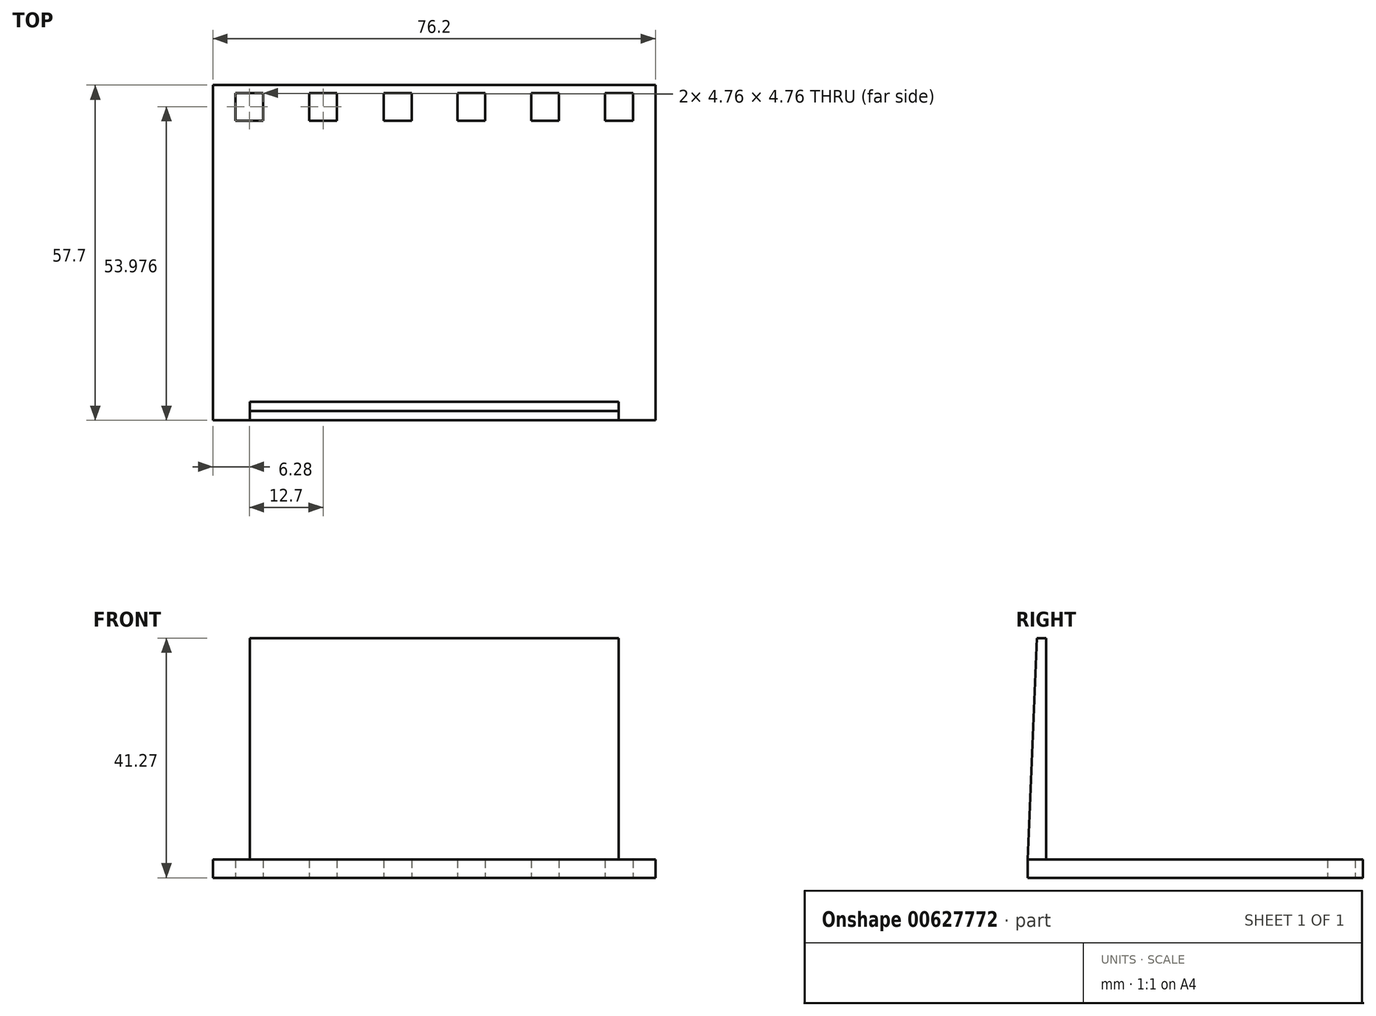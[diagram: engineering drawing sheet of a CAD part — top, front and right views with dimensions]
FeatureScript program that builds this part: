
annotation { "Feature Type Name" : "Feature", "Feature Type Description" : "" }
export const myFeature = defineFeature(function(context is Context, id is Id, definition is map)
    precondition{}
    {
        {
            var Q0;
            Q0=qCreatedBy(makeId("Top.planeOp"),FACE);
            var sketch = newSketch(context, id + "F0", { "sketchPlane" : qUnion([Q0])});
            skLineSegment(sketch, "E0.bottom", {"start": v(38.1, 31.75) * mm, "end": v(-38.1, 31.75) * mm});
            skLineSegment(sketch, "E0.top", {"start": v(38.1, -31.75) * mm, "end": v(-38.1, -31.75) * mm});
            skLineSegment(sketch, "E0.left", {"start": v(38.1, 31.75) * mm, "end": v(38.1, -31.75) * mm});
            skLineSegment(sketch, "E0.right", {"start": v(-38.1, 31.75) * mm, "end": v(-38.1, -31.75) * mm});
            skPoint(sketch, "E0.middle", {"position": v(0, 0) * mm});
            skLineSegment(sketch, "E1.bottom", {"start": v(-34.2, 27.79) * mm, "end": v(-29.44, 27.79) * mm});
            skLineSegment(sketch, "E1.top", {"start": v(-34.2, 23.03) * mm, "end": v(-29.44, 23.03) * mm});
            skLineSegment(sketch, "E1.left", {"start": v(-34.2, 27.79) * mm, "end": v(-34.2, 23.03) * mm});
            skLineSegment(sketch, "E1.right", {"start": v(-29.44, 27.79) * mm, "end": v(-29.44, 23.03) * mm});
            skLineSegment(sketch, "E2", {"start": v(-34.2, 27.79) * mm, "end": v(-38.1, 27.79) * mm});
            skLineSegment(sketch, "E3", {"start": v(-34.2, 27.79) * mm, "end": v(-34.2, 31.75) * mm});
            skLineSegment(sketch, "E4", {"start": v(-29.44, 27.79) * mm, "end": v(-21.5, 27.79) * mm});
            skLineSegment(sketch, "E5.bottom", {"start": v(-21.5, 27.79) * mm, "end": v(-16.74, 27.79) * mm});
            skLineSegment(sketch, "E5.top", {"start": v(-21.5, 23.03) * mm, "end": v(-16.74, 23.03) * mm});
            skLineSegment(sketch, "E5.left", {"start": v(-21.5, 27.79) * mm, "end": v(-21.5, 23.03) * mm});
            skLineSegment(sketch, "E5.right", {"start": v(-16.74, 27.79) * mm, "end": v(-16.74, 23.03) * mm});
            skLineSegment(sketch, "E6", {"start": v(-34.2, 23.03) * mm, "end": v(-34.2, 15.09) * mm});
            skLineSegment(sketch, "E7.left", {"start": v(-34.2, 15.09) * mm, "end": v(-34.2, 10.33) * mm});
            skLineSegment(sketch, "E8", {"start": v(-16.74, 27.79) * mm, "end": v(-8.66, 27.79) * mm});
            skLineSegment(sketch, "E9", {"start": v(-8.66, 27.79) * mm, "end": v(-3.9, 27.79) * mm});
            skLineSegment(sketch, "E10", {"start": v(-3.9, 27.79) * mm, "end": v(4.04, 27.79) * mm});
            skLineSegment(sketch, "E11", {"start": v(4.04, 27.79) * mm, "end": v(8.8, 27.79) * mm});
            skLineSegment(sketch, "E12", {"start": v(8.8, 27.79) * mm, "end": v(16.74, 27.79) * mm});
            skLineSegment(sketch, "E13", {"start": v(16.74, 27.79) * mm, "end": v(21.5, 27.79) * mm});
            skLineSegment(sketch, "E14", {"start": v(21.5, 27.79) * mm, "end": v(29.44, 27.79) * mm});
            skLineSegment(sketch, "E15", {"start": v(29.44, 27.79) * mm, "end": v(34.2, 27.79) * mm});
            skLineSegment(sketch, "E16", {"start": v(34.2, 27.79) * mm, "end": v(38.1, 27.79) * mm});
            skLineSegment(sketch, "E17", {"start": v(-34.2, 10.33) * mm, "end": v(-34.2, 2.39) * mm});
            skLineSegment(sketch, "E18", {"start": v(-34.2, 2.39) * mm, "end": v(-34.2, -2.37) * mm});
            skLineSegment(sketch, "E19", {"start": v(-34.2, -2.37) * mm, "end": v(-34.2, -10.31) * mm});
            skLineSegment(sketch, "E20", {"start": v(-34.2, -10.31) * mm, "end": v(-34.2, -15.07) * mm});
            skLineSegment(sketch, "E21", {"start": v(-34.2, -15.07) * mm, "end": v(-34.2, -23.01) * mm});
            skLineSegment(sketch, "E22", {"start": v(-34.2, -23.01) * mm, "end": v(-34.2, -27.77) * mm});
            skLineSegment(sketch, "E23", {"start": v(-34.2, -27.77) * mm, "end": v(-34.2, -31.75) * mm});
            skPoint(sketch, "E24.oppositeSnap0", {"position": v(-19.12, 23.03) * mm});
            skLineSegment(sketch, "E24.bottom", {"start": v(-8.66, 27.79) * mm, "end": v(-3.88, 27.79) * mm});
            skLineSegment(sketch, "E24.top", {"start": v(-8.66, 23.03) * mm, "end": v(-3.88, 23.03) * mm});
            skLineSegment(sketch, "E24.left", {"start": v(-8.66, 27.79) * mm, "end": v(-8.66, 23.03) * mm});
            skLineSegment(sketch, "E24.right", {"start": v(-3.88, 27.79) * mm, "end": v(-3.88, 23.03) * mm});
            skLineSegment(sketch, "E25.bottom", {"start": v(4.04, 27.79) * mm, "end": v(8.79, 27.79) * mm});
            skLineSegment(sketch, "E25.top", {"start": v(4.04, 23.03) * mm, "end": v(8.79, 23.03) * mm});
            skLineSegment(sketch, "E25.left", {"start": v(4.04, 27.79) * mm, "end": v(4.04, 23.03) * mm});
            skLineSegment(sketch, "E25.right", {"start": v(8.79, 27.79) * mm, "end": v(8.79, 23.03) * mm});
            skPoint(sketch, "E26.oppositeSnap0", {"position": v(6.41, 23.03) * mm});
            skLineSegment(sketch, "E26.bottom", {"start": v(16.74, 27.79) * mm, "end": v(21.46, 27.79) * mm});
            skLineSegment(sketch, "E26.top", {"start": v(16.74, 23.03) * mm, "end": v(21.46, 23.03) * mm});
            skLineSegment(sketch, "E26.left", {"start": v(16.74, 27.79) * mm, "end": v(16.74, 23.03) * mm});
            skLineSegment(sketch, "E26.right", {"start": v(21.46, 27.79) * mm, "end": v(21.46, 23.03) * mm});
            skLineSegment(sketch, "E27.bottom", {"start": v(29.44, 27.79) * mm, "end": v(34.23, 27.79) * mm});
            skLineSegment(sketch, "E27.top", {"start": v(29.44, 23.03) * mm, "end": v(34.23, 23.03) * mm});
            skLineSegment(sketch, "E27.left", {"start": v(29.44, 27.79) * mm, "end": v(29.44, 23.03) * mm});
            skLineSegment(sketch, "E27.right", {"start": v(34.23, 27.79) * mm, "end": v(34.23, 23.03) * mm});
            skSolve(sketch);
        }
        {
            var Q0;
            Q0 = qSketchRegion(id + "F0", true);
            extrude(context, id + "F1", {"entities" : qUnion([Q0]), "depth" : 3.17 * mm, "offsetDistance" : 25.4 * mm});
        }
        {
            var Q0;
            Q0=makeQuery(id+"F1.opExtrude","CAP_FACE",FACE,{"disambiguationData":[OSD([sQuery(id+"F0.wireOp",EDGE,"E0.bottom"),sQuery(id+"F0.wireOp",EDGE,"E0.top"),sQuery(id+"F0.wireOp",EDGE,"E0.left"),sQuery(id+"F0.wireOp",EDGE,"E0.right"),sQuery(id+"F0.wireOp",EDGE,"E1.bottom"),sQuery(id+"F0.wireOp",EDGE,"E1.top"),sQuery(id+"F0.wireOp",EDGE,"E1.left"),sQuery(id+"F0.wireOp",EDGE,"E1.right"),sQuery(id+"F0.wireOp",EDGE,"E5.bottom"),sQuery(id+"F0.wireOp",EDGE,"E5.top"),sQuery(id+"F0.wireOp",EDGE,"E5.left"),sQuery(id+"F0.wireOp",EDGE,"E5.right"),sQuery(id+"F0.wireOp",EDGE,"E24.bottom"),sQuery(id+"F0.wireOp",EDGE,"E24.top"),sQuery(id+"F0.wireOp",EDGE,"E24.left"),sQuery(id+"F0.wireOp",EDGE,"E24.right"),sQuery(id+"F0.wireOp",EDGE,"E25.bottom"),sQuery(id+"F0.wireOp",EDGE,"E25.top"),sQuery(id+"F0.wireOp",EDGE,"E25.left"),sQuery(id+"F0.wireOp",EDGE,"E25.right"),sQuery(id+"F0.wireOp",EDGE,"E26.bottom"),sQuery(id+"F0.wireOp",EDGE,"E26.top"),sQuery(id+"F0.wireOp",EDGE,"E26.left"),sQuery(id+"F0.wireOp",EDGE,"E26.right"),sQuery(id+"F0.wireOp",EDGE,"E27.bottom"),sQuery(id+"F0.wireOp",EDGE,"E27.top"),sQuery(id+"F0.wireOp",EDGE,"E27.left"),sQuery(id+"F0.wireOp",EDGE,"E27.right")])],"isStart":false});
            var sketch = newSketch(context, id + "F2", { "sketchPlane" : qUnion([Q0])});
            skLineSegment(sketch, "E28", {"start": v(-31.75, -31.75) * mm, "end": v(31.75, -31.75) * mm});
            skLineSegment(sketch, "E29", {"start": v(-31.75, -31.75) * mm, "end": v(-31.75, -25.4) * mm});
            skLineSegment(sketch, "E30", {"start": v(-31.75, -25.4) * mm, "end": v(31.75, -25.4) * mm});
            skLineSegment(sketch, "E31", {"start": v(-31.75, -28.57) * mm, "end": v(-38.1, -28.57) * mm});
            skLineSegment(sketch, "E32", {"start": v(31.75, -25.4) * mm, "end": v(31.75, -31.75) * mm});
            skLineSegment(sketch, "E33", {"start": v(31.75, -28.57) * mm, "end": v(38.1, -28.57) * mm});
            skSolve(sketch);
        }
        {
            var Q0;
            Q0 = qSketchRegion(id + "F2", true);
            extrude(context, id + "F3", {"entities" : qUnion([Q0]), "operationType" : NewBodyOperationType.ADD, "depth" : 38.1 * mm, "offsetDistance" : 25.4 * mm});
        }
        {
            var Q0;
            Q0=makeQuery(id+"F3.opExtrude","SWEPT_FACE",FACE,{"disambiguationData":[OSD([sQuery(id+"F2.wireOp",EDGE,"E29")])]});
            var sketch = newSketch(context, id + "F4", { "sketchPlane" : qUnion([Q0])});
            skLineSegment(sketch, "E34", {"start": v(28.57, 41.27) * mm, "end": v(31.75, 3.18) * mm});
            skLineSegment(sketch, "E35", {"start": v(31.75, 3.18) * mm, "end": v(31.75, 41.27) * mm});
            skLineSegment(sketch, "E36", {"start": v(31.75, 41.27) * mm, "end": v(28.57, 41.27) * mm});
            skSolve(sketch);
        }
        {
            var Q0;
            Q0=makeQuery(id+"F4.imprint","IMPRINT",FACE,{"disambiguationData":[TD([[makeQuery(id+"F4.imprint","IMPRINT",EDGE,{"derivedFrom":sQuery(id+"F4.wireOp",EDGE,"E34")}),1.0]])]});
            extrude(context, id + "F5", {"entities" : qUnion([Q0]), "operationType" : NewBodyOperationType.REMOVE, "oppositeDirection" : true, "depth" : 64.26 * mm, "offsetDistance" : 25.4 * mm});
        }
        {
            var Q0;
            Q0=makeQuery(id+"F3.opExtrude","SWEPT_FACE",FACE,{"disambiguationData":[OSD([sQuery(id+"F2.wireOp",EDGE,"E32")])]});
            var sketch = newSketch(context, id + "F6", { "sketchPlane" : qUnion([Q0])});
            skLineSegment(sketch, "E37", {"start": v(-25.4, 3.18) * mm, "end": v(-25.4, 41.27) * mm});
            skLineSegment(sketch, "E38", {"start": v(-25.4, 41.27) * mm, "end": v(-26.99, 41.27) * mm});
            skLineSegment(sketch, "E39", {"start": v(-26.99, 41.28) * mm, "end": v(-28.57, 3.17) * mm});
            skLineSegment(sketch, "E40", {"start": v(-28.57, 3.17) * mm, "end": v(-25.4, 3.18) * mm});
            skSolve(sketch);
        }
        {
            var Q0;
            {var subQ0=sQuery(id+"F6.wireOp",EDGE,"E39");Q0=makeQuery(id+"F6.imprint","IMPRINT",FACE,{"disambiguationData":[TD([[makeQuery(id+"F6.imprint","IMPRINT",EDGE,{"derivedFrom":subQ0}),-1.0]])]});}
            extrude(context, id + "F7", {"entities" : qUnion([Q0]), "operationType" : NewBodyOperationType.REMOVE, "oppositeDirection" : true, "depth" : 63.5 * mm, "offsetDistance" : 25.4 * mm});
        }
        {
            var Q0;
            {var subQ0=sQuery(id+"F2.wireOp",EDGE,"E32");var subQ1=makeQuery(id+"F3.opExtrude","CAP_EDGE",EDGE,{"disambiguationData":[OSD([subQ0])],"isStart":true});Q0=makeQuery(id+"F7.boolean.opBoolean","MERGE",FACE,{"derivedFrom":[makeQuery(id+"F1.opExtrude","CAP_FACE",FACE,{"disambiguationData":[OSD([sQuery(id+"F0.wireOp",EDGE,"E0.bottom"),sQuery(id+"F0.wireOp",EDGE,"E0.top"),sQuery(id+"F0.wireOp",EDGE,"E0.left"),sQuery(id+"F0.wireOp",EDGE,"E0.right"),sQuery(id+"F0.wireOp",EDGE,"E1.bottom"),sQuery(id+"F0.wireOp",EDGE,"E1.top"),sQuery(id+"F0.wireOp",EDGE,"E1.left"),sQuery(id+"F0.wireOp",EDGE,"E1.right"),sQuery(id+"F0.wireOp",EDGE,"E5.bottom"),sQuery(id+"F0.wireOp",EDGE,"E5.top"),sQuery(id+"F0.wireOp",EDGE,"E5.left"),sQuery(id+"F0.wireOp",EDGE,"E5.right"),sQuery(id+"F0.wireOp",EDGE,"E24.bottom"),sQuery(id+"F0.wireOp",EDGE,"E24.top"),sQuery(id+"F0.wireOp",EDGE,"E24.left"),sQuery(id+"F0.wireOp",EDGE,"E24.right"),sQuery(id+"F0.wireOp",EDGE,"E25.bottom"),sQuery(id+"F0.wireOp",EDGE,"E25.top"),sQuery(id+"F0.wireOp",EDGE,"E25.left"),sQuery(id+"F0.wireOp",EDGE,"E25.right"),sQuery(id+"F0.wireOp",EDGE,"E26.bottom"),sQuery(id+"F0.wireOp",EDGE,"E26.top"),sQuery(id+"F0.wireOp",EDGE,"E26.left"),sQuery(id+"F0.wireOp",EDGE,"E26.right"),sQuery(id+"F0.wireOp",EDGE,"E27.bottom"),sQuery(id+"F0.wireOp",EDGE,"E27.top"),sQuery(id+"F0.wireOp",EDGE,"E27.left"),sQuery(id+"F0.wireOp",EDGE,"E27.right")])],"isStart":false}),makeQuery(id+"F7.opExtrude","SWEPT_FACE",FACE,{"disambiguationData":[OSD([subQ0]),TDD([makeQuery(id+"F6.imprint","IMPRINT",EDGE,{"disambiguationData":[TD([[makeQuery(id+"F6.imprint","INTERSECT",VERTEX,{"derivedFrom":[subQ1,makeQuery(id+"F5.boolean.opBoolean","INTERSECT",EDGE,{"derivedFrom":[makeQuery(id+"F3.opExtrude","SWEPT_FACE",FACE,{"disambiguationData":[OSD([subQ0])]}),makeQuery(id+"F5.opExtrude","SWEPT_FACE",FACE,{"disambiguationData":[OSD([sQuery(id+"F4.wireOp",EDGE,"E34")])]})]})]}),1.0]])],"derivedFrom":subQ1})])]})]});}
            var sketch = newSketch(context, id + "F8", { "sketchPlane" : qUnion([Q0])});
            skLineSegment(sketch, "E41", {"start": v(-31.75, -28.57) * mm, "end": v(38.1, -28.57) * mm});
            skLineSegment(sketch, "E42", {"start": v(38.1, -28.57) * mm, "end": v(38.1, -31.75) * mm});
            skLineSegment(sketch, "E43", {"start": v(38.1, -31.75) * mm, "end": v(-38.1, -31.75) * mm});
            skLineSegment(sketch, "E44", {"start": v(-31.75, -28.57) * mm, "end": v(-38.1, -28.57) * mm});
            skLineSegment(sketch, "E45", {"start": v(-38.1, -28.57) * mm, "end": v(-38.1, -31.75) * mm});
            skSolve(sketch);
        }
        {
            var Q0;
            Q0 = qSketchRegion(id + "F8", true);
            extrude(context, id + "F9", {"entities" : qUnion([Q0]), "operationType" : NewBodyOperationType.REMOVE, "oppositeDirection" : true, "depth" : 25.4 * mm, "offsetDistance" : 25.4 * mm});
        }
        {
            var Q0;
            {var subQ0=sQuery(id+"F2.wireOp",EDGE,"E32");var subQ1=makeQuery(id+"F3.opExtrude","CAP_EDGE",EDGE,{"disambiguationData":[OSD([subQ0])],"isStart":true});Q0=makeQuery(id+"F7.boolean.opBoolean","MERGE",FACE,{"derivedFrom":[makeQuery(id+"F1.opExtrude","CAP_FACE",FACE,{"disambiguationData":[OSD([sQuery(id+"F0.wireOp",EDGE,"E0.bottom"),sQuery(id+"F0.wireOp",EDGE,"E0.top"),sQuery(id+"F0.wireOp",EDGE,"E0.left"),sQuery(id+"F0.wireOp",EDGE,"E0.right"),sQuery(id+"F0.wireOp",EDGE,"E1.bottom"),sQuery(id+"F0.wireOp",EDGE,"E1.top"),sQuery(id+"F0.wireOp",EDGE,"E1.left"),sQuery(id+"F0.wireOp",EDGE,"E1.right"),sQuery(id+"F0.wireOp",EDGE,"E5.bottom"),sQuery(id+"F0.wireOp",EDGE,"E5.top"),sQuery(id+"F0.wireOp",EDGE,"E5.left"),sQuery(id+"F0.wireOp",EDGE,"E5.right"),sQuery(id+"F0.wireOp",EDGE,"E24.bottom"),sQuery(id+"F0.wireOp",EDGE,"E24.top"),sQuery(id+"F0.wireOp",EDGE,"E24.left"),sQuery(id+"F0.wireOp",EDGE,"E24.right"),sQuery(id+"F0.wireOp",EDGE,"E25.bottom"),sQuery(id+"F0.wireOp",EDGE,"E25.top"),sQuery(id+"F0.wireOp",EDGE,"E25.left"),sQuery(id+"F0.wireOp",EDGE,"E25.right"),sQuery(id+"F0.wireOp",EDGE,"E26.bottom"),sQuery(id+"F0.wireOp",EDGE,"E26.top"),sQuery(id+"F0.wireOp",EDGE,"E26.left"),sQuery(id+"F0.wireOp",EDGE,"E26.right"),sQuery(id+"F0.wireOp",EDGE,"E27.bottom"),sQuery(id+"F0.wireOp",EDGE,"E27.top"),sQuery(id+"F0.wireOp",EDGE,"E27.left"),sQuery(id+"F0.wireOp",EDGE,"E27.right")])],"isStart":false}),makeQuery(id+"F7.opExtrude","SWEPT_FACE",FACE,{"disambiguationData":[OSD([subQ0]),TDD([makeQuery(id+"F6.imprint","IMPRINT",EDGE,{"disambiguationData":[TD([[makeQuery(id+"F6.imprint","INTERSECT",VERTEX,{"derivedFrom":[subQ1,makeQuery(id+"F5.boolean.opBoolean","INTERSECT",EDGE,{"derivedFrom":[makeQuery(id+"F3.opExtrude","SWEPT_FACE",FACE,{"disambiguationData":[OSD([subQ0])]}),makeQuery(id+"F5.opExtrude","SWEPT_FACE",FACE,{"disambiguationData":[OSD([sQuery(id+"F4.wireOp",EDGE,"E34")])]})]})]}),1.0]])],"derivedFrom":subQ1})])]})]});}
            var sketch = newSketch(context, id + "F10", { "sketchPlane" : qUnion([Q0])});
            skLineSegment(sketch, "E46", {"start": v(-38.1, 31.75) * mm, "end": v(-38.1, 29.13) * mm});
            skLineSegment(sketch, "E47", {"start": v(-38.1, 29.13) * mm, "end": v(38.1, 29.13) * mm});
            skLineSegment(sketch, "E48", {"start": v(38.1, 29.13) * mm, "end": v(38.1, 31.75) * mm});
            skLineSegment(sketch, "E49", {"start": v(38.1, 31.75) * mm, "end": v(-38.1, 31.75) * mm});
            skSolve(sketch);
        }
        {
            var Q0;
            Q0 = qSketchRegion(id + "F10", true);
            extrude(context, id + "F11", {"entities" : qUnion([Q0]), "operationType" : NewBodyOperationType.REMOVE, "oppositeDirection" : true, "depth" : 25.4 * mm, "offsetDistance" : 25.4 * mm});
        }
    });
